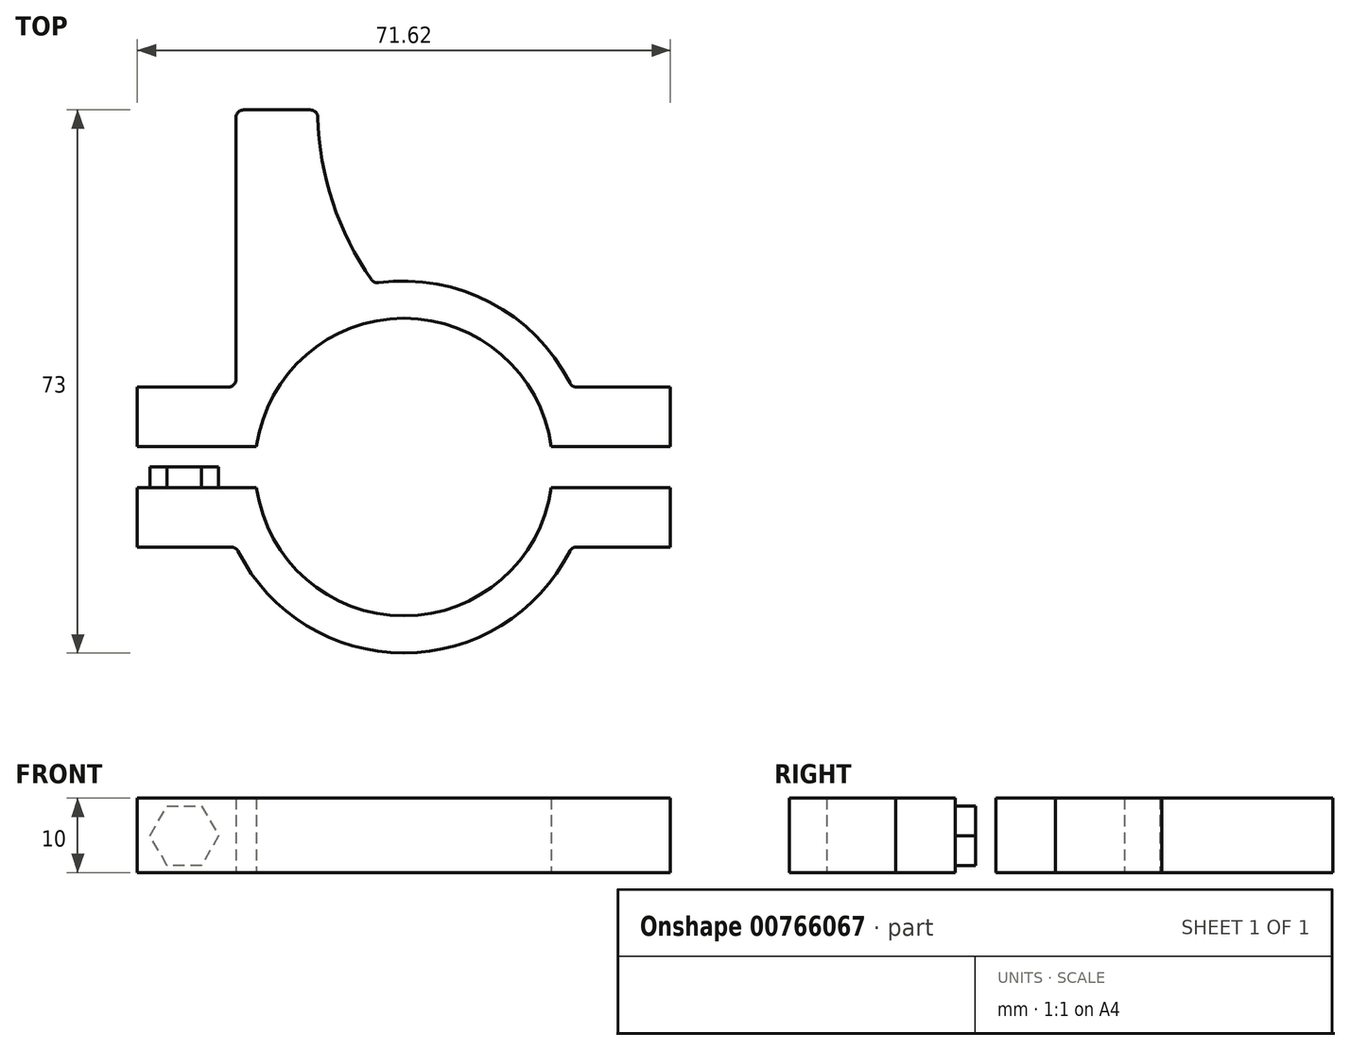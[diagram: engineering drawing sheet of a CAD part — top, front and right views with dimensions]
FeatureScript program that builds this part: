
annotation { "Feature Type Name" : "Feature", "Feature Type Description" : "" }
export const myFeature = defineFeature(function(context is Context, id is Id, definition is map)
    precondition{}
    {
        {
            var Q0;
            Q0=qCreatedBy(makeId("Top.planeOp"),FACE);
            var sketch = newSketch(context, id + "F0", { "sketchPlane" : qUnion([Q0])});
            skArc(sketch, "E0", {"start": v(-19.81, -2.75) * mm, "mid": v(0, -20) * mm, "end": v(19.81, -2.75) * mm});
            skArc(sketch, "E1.0", {"start": v(-22.3, -11.3) * mm, "mid": v(0, -25) * mm, "end": v(22.3, -11.3) * mm});
            skArc(sketch, "E2.trimOffspring", {"start": v(19.81, 2.75) * mm, "mid": v(0, 20) * mm, "end": v(-19.81, 2.75) * mm});
            skArc(sketch, "E3.trimOffspring", {"start": v(22.3, 11.3) * mm, "mid": v(11.6, 22.14) * mm, "end": v(-3.4, 24.77) * mm});
            skLineSegment(sketch, "E4", {"start": v(-24.85, 2.75) * mm, "end": v(-35.81, 2.75) * mm});
            skLineSegment(sketch, "E5", {"start": v(-35.81, 2.75) * mm, "end": v(-35.81, 10.75) * mm});
            skLineSegment(sketch, "E6", {"start": v(-35.81, 10.75) * mm, "end": v(-23.57, 10.75) * mm});
            skPoint(sketch, "E7.orphan", {"position": v(-19.81, 10.75) * mm});
            skLineSegment(sketch, "E8", {"start": v(-24.85, -2.75) * mm, "end": v(-35.81, -2.75) * mm});
            skLineSegment(sketch, "E9", {"start": v(-35.81, -2.75) * mm, "end": v(-35.81, -10.75) * mm});
            skLineSegment(sketch, "E10", {"start": v(-35.81, -10.75) * mm, "end": v(-23.2, -10.75) * mm});
            skPoint(sketch, "E11.orphan", {"position": v(-19.81, -10.75) * mm});
            skLineSegment(sketch, "E12", {"start": v(24.85, 2.75) * mm, "end": v(35.81, 2.75) * mm});
            skLineSegment(sketch, "E13", {"start": v(35.81, 2.75) * mm, "end": v(35.81, 10.75) * mm});
            skLineSegment(sketch, "E14", {"start": v(35.81, 10.75) * mm, "end": v(23.2, 10.75) * mm});
            skLineSegment(sketch, "E15", {"start": v(24.85, -2.75) * mm, "end": v(35.81, -2.75) * mm});
            skLineSegment(sketch, "E16", {"start": v(35.81, -2.75) * mm, "end": v(35.81, -10.75) * mm});
            skLineSegment(sketch, "E17", {"start": v(35.81, -10.75) * mm, "end": v(23.2, -10.75) * mm});
            skPoint(sketch, "E18.orphan", {"position": v(19.81, 10.75) * mm});
            skPoint(sketch, "E19.orphan", {"position": v(19.81, -10.75) * mm});
            skPoint(sketch, "E20.end.orphan", {"position": v(24.85, 2.75) * mm});
            skLineSegment(sketch, "E21", {"start": v(-24.85, 2.75) * mm, "end": v(-19.81, 2.75) * mm});
            skLineSegment(sketch, "E22", {"start": v(-24.85, -2.75) * mm, "end": v(-19.81, -2.75) * mm});
            skLineSegment(sketch, "E23", {"start": v(19.81, 2.75) * mm, "end": v(24.85, 2.75) * mm});
            skLineSegment(sketch, "E24", {"start": v(19.81, -2.75) * mm, "end": v(24.85, -2.75) * mm});
            skLineSegment(sketch, "E25", {"start": v(-22.57, 11.75) * mm, "end": v(-22.57, 47) * mm});
            skLineSegment(sketch, "E26", {"start": v(-21.57, 48) * mm, "end": v(-12.56, 48) * mm});
            skPoint(sketch, "E27.start.orphan", {"position": v(0, 20) * mm});
            skArc(sketch, "E28", {"start": v(-11.56, 47.02) * mm, "mid": v(-9.57, 35.57) * mm, "end": v(-4.35, 25.18) * mm});
            skPoint(sketch, "E29.visualSharp", {"position": v(-4, 24.68) * mm});
            skArc(sketch, "E29.filletArc", {"start": v(-4.35, 25.18) * mm, "mid": v(-3.93, 24.84) * mm, "end": v(-3.4, 24.77) * mm});
            skPoint(sketch, "E30.visualSharp", {"position": v(-22.57, 10.75) * mm});
            skArc(sketch, "E30.filletArc", {"start": v(-23.57, 10.75) * mm, "mid": v(-22.86, 11.04) * mm, "end": v(-22.57, 11.75) * mm});
            skPoint(sketch, "E31.visualSharp", {"position": v(-22.57, -10.75) * mm});
            skArc(sketch, "E31.filletArc", {"start": v(-22.3, -11.3) * mm, "mid": v(-22.67, -10.9) * mm, "end": v(-23.2, -10.75) * mm});
            skPoint(sketch, "E32.visualSharp", {"position": v(22.57, -10.75) * mm});
            skArc(sketch, "E32.filletArc", {"start": v(23.2, -10.75) * mm, "mid": v(22.67, -10.9) * mm, "end": v(22.3, -11.3) * mm});
            skPoint(sketch, "E33.visualSharp", {"position": v(22.57, 10.75) * mm});
            skArc(sketch, "E33.filletArc", {"start": v(22.3, 11.3) * mm, "mid": v(22.67, 10.9) * mm, "end": v(23.2, 10.75) * mm});
            skPoint(sketch, "E34.visualSharp", {"position": v(-11.57, 48) * mm});
            skArc(sketch, "E34.filletArc", {"start": v(-11.56, 47.02) * mm, "mid": v(-11.86, 47.72) * mm, "end": v(-12.56, 48) * mm});
            skPoint(sketch, "E35.visualSharp", {"position": v(-22.57, 48) * mm});
            skArc(sketch, "E35.filletArc", {"start": v(-21.57, 48) * mm, "mid": v(-22.28, 47.7) * mm, "end": v(-22.57, 47) * mm});
            skSolve(sketch);
        }
        {
            var Q0;
            Q0=makeQuery(id+"F0.imprint","IMPRINT",FACE,{"disambiguationData":[TD([[makeQuery(id+"F0.imprint","IMPRINT",EDGE,{"derivedFrom":sQuery(id+"F0.wireOp",EDGE,"E2.trimOffspring")}),-1.0]])]});
            var Q1;
            Q1=makeQuery(id+"F0.imprint","IMPRINT",FACE,{"disambiguationData":[TD([[makeQuery(id+"F0.imprint","IMPRINT",EDGE,{"derivedFrom":sQuery(id+"F0.wireOp",EDGE,"E0")}),-1.0]])]});
            extrude(context, id + "F1", {"entities" : qUnion([Q0, Q1]), "depth" : 10 * mm, "offsetDistance" : 25 * mm});
        }
        {
            var Q0;
            Q0=qCreatedBy(makeId("Front.planeOp"),FACE);
            var sketch = newSketch(context, id + "F2", { "sketchPlane" : qUnion([Q0])});
            skCircle(sketch, "E36.cCircle", {"center": v(-29.5, 4.95) * mm, "radius": 4 * mm, "construction": true});
            skLineSegment(sketch, "E36.0", {"start": v(-34.13, 4.94) * mm, "end": v(-31.82, 8.95) * mm});
            skLineSegment(sketch, "E36.1", {"start": v(-31.82, 8.95) * mm, "end": v(-27.2, 8.95) * mm});
            skLineSegment(sketch, "E36.2", {"start": v(-27.2, 8.95) * mm, "end": v(-24.89, 4.96) * mm});
            skLineSegment(sketch, "E36.3", {"start": v(-24.89, 4.96) * mm, "end": v(-27.2, 0.95) * mm});
            skLineSegment(sketch, "E36.4", {"start": v(-27.2, 0.95) * mm, "end": v(-31.81, 0.95) * mm});
            skLineSegment(sketch, "E36.5", {"start": v(-31.81, 0.95) * mm, "end": v(-34.13, 4.94) * mm});
            skPoint(sketch, "E36.0.midPoint", {"position": v(-32.98, 6.94) * mm});
            skSolve(sketch);
        }
        {
            var Q0;
            Q0 = qSketchRegion(id + "F2", true);
            extrude(context, id + "F3", {"entities" : qUnion([Q0]), "operationType" : NewBodyOperationType.ADD, "depth" : 3.5 * mm, "offsetDistance" : 25 * mm});
        }
    });
